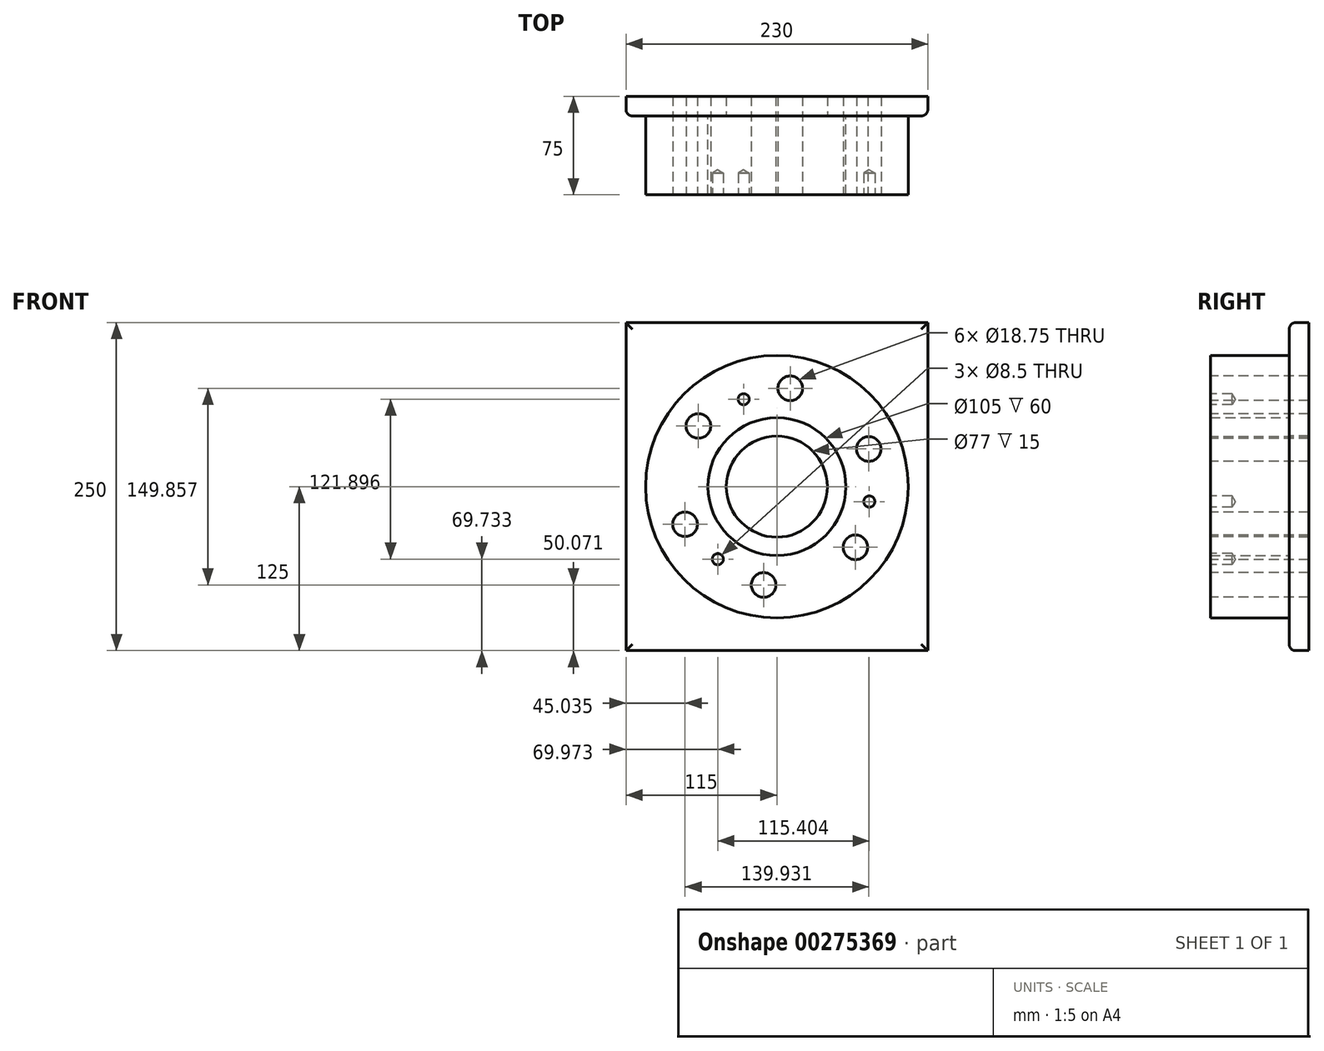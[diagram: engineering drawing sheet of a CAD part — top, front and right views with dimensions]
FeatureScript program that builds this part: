
annotation { "Feature Type Name" : "Feature", "Feature Type Description" : "" }
export const myFeature = defineFeature(function(context is Context, id is Id, definition is map)
    precondition{}
    {
        {
            var Q0;
            Q0=qCreatedBy(makeId("Front.planeOp"),FACE);
            var sketch = newSketch(context, id + "F0", { "sketchPlane" : qUnion([Q0])});
            skCircle(sketch, "E0", {"center": v(0, 0) * mm, "radius": 100 * mm});
            skCircle(sketch, "E1", {"center": v(0, 0) * mm, "radius": 52.5 * mm});
            skSolve(sketch);
        }
        {
            var Q0;
            Q0 = qSketchRegion(id + "F0", true);
            extrude(context, id + "F1", {"entities" : qUnion([Q0]), "depth" : 60 * mm});
        }
        {
            var Q0;
            Q0=makeQuery(id+"F1.opExtrude","CAP_FACE",FACE,{"disambiguationData":[OSD([sQuery(id+"F0.wireOp",EDGE,"E0"),sQuery(id+"F0.wireOp",EDGE,"E1")])],"isStart":false});
            var sketch = newSketch(context, id + "F2", { "sketchPlane" : qUnion([Q0])});
            skCircle(sketch, "E2", {"center": v(-59.81, 46.25) * mm, "radius": 9.38 * mm});
            skCircle(sketch, "E3.1.0", {"center": v(-69.97, -28.67) * mm, "radius": 9.38 * mm});
            skCircle(sketch, "E3.2.0", {"center": v(-10.15, -74.93) * mm, "radius": 9.38 * mm});
            skCircle(sketch, "E3.3.0", {"center": v(59.81, -46.25) * mm, "radius": 9.38 * mm});
            skCircle(sketch, "E3.4.0", {"center": v(69.97, 28.67) * mm, "radius": 9.38 * mm});
            skCircle(sketch, "E3.5.0", {"center": v(10.15, 74.93) * mm, "radius": 9.38 * mm});
            skPoint(sketch, "E3.center", {"position": v(0, 0) * mm});
            skSolve(sketch);
        }
        {
            var Q0;
            Q0=makeQuery(id+"F1.opExtrude","CAP_FACE",FACE,{"disambiguationData":[OSD([sQuery(id+"F0.wireOp",EDGE,"E0"),sQuery(id+"F0.wireOp",EDGE,"E1")])],"isStart":true});
            var sketch = newSketch(context, id + "F3", { "sketchPlane" : qUnion([Q0])});
            skLineSegment(sketch, "E4.bottom", {"start": v(-115, -125) * mm, "end": v(115, -125) * mm});
            skLineSegment(sketch, "E4.top", {"start": v(-115, 125) * mm, "end": v(115, 125) * mm});
            skLineSegment(sketch, "E4.left", {"start": v(-115, -125) * mm, "end": v(-115, 125) * mm});
            skLineSegment(sketch, "E4.right", {"start": v(115, -125) * mm, "end": v(115, 125) * mm});
            skSolve(sketch);
        }
        {
            var Q0;
            Q0 = qSketchRegion(id + "F3", true);
            extrude(context, id + "F4", {"entities" : qUnion([Q0]), "operationType" : NewBodyOperationType.ADD, "depth" : 15 * mm});
        }
        {
            var Q0;
            Q0 = qSketchRegion(id + "F2", true);
            extrude(context, id + "F5", {"entities" : qUnion([Q0]), "operationType" : NewBodyOperationType.REMOVE, "endBound" : BoundingType.THROUGH_ALL, "oppositeDirection" : true, "depth" : 25 * mm});
        }
        {
            var Q0;
            Q0=makeQuery(id+"F4.boolean.opBoolean","SPLIT",FACE,{"disambiguationData":[TD([makeQuery(id+"F1.opExtrude","SWEPT_FACE",FACE,{"disambiguationData":[OSD([sQuery(id+"F0.wireOp",EDGE,"E1")])]})])],"derivedFrom":makeQuery(id+"F4.opExtrude","CAP_FACE",FACE,{"disambiguationData":[OSD([sQuery(id+"F3.wireOp",EDGE,"E4.bottom"),sQuery(id+"F3.wireOp",EDGE,"E4.top"),sQuery(id+"F3.wireOp",EDGE,"E4.left"),sQuery(id+"F3.wireOp",EDGE,"E4.right")])],"isStart":true})});
            var sketch = newSketch(context, id + "F6", { "sketchPlane" : qUnion([Q0])});
            skCircle(sketch, "E5", {"center": v(0, 0) * mm, "radius": 38.5 * mm});
            skSolve(sketch);
        }
        {
            var Q0;
            Q0 = qSketchRegion(id + "F6", true);
            extrude(context, id + "F7", {"entities" : qUnion([Q0]), "operationType" : NewBodyOperationType.REMOVE, "endBound" : BoundingType.THROUGH_ALL, "oppositeDirection" : true, "depth" : 25 * mm});
        }
        {
            var Q0;
            Q0=makeQuery(id+"F1.opExtrude","CAP_FACE",FACE,{"disambiguationData":[OSD([sQuery(id+"F0.wireOp",EDGE,"E0"),sQuery(id+"F0.wireOp",EDGE,"E1")])],"isStart":false});
            var sketch = newSketch(context, id + "F8", { "sketchPlane" : qUnion([Q0])});
            skPoint(sketch, "E6", {"position": v(-45.03, -55.27) * mm});
            skPoint(sketch, "E7.1.0", {"position": v(70.38, -11.36) * mm});
            skPoint(sketch, "E7.2.0", {"position": v(-25.35, 66.63) * mm});
            skPoint(sketch, "E7.center", {"position": v(0, 0) * mm});
            skSolve(sketch);
        }
        {
            var Q0;
            Q0=sQuery(id+"F8.wireOp",VERTEX,"E6");
            var Q1;
            Q1=sQuery(id+"F8.wireOp",VERTEX,"E7.2.0");
            var Q2;
            Q2=sQuery(id+"F8.wireOp",VERTEX,"E7.1.0");
            var Q3;
            Q3=makeQuery(id+"F1.opExtrude","SWEPT_BODY",BODY,{"disambiguationData":[OSD([sQuery(id+"F0.wireOp",EDGE,"E0"),sQuery(id+"F0.wireOp",EDGE,"E1")])]});
            hole(context, id + "F9", {"style" : HoleStyle.SIMPLE, "endStyle" : HoleEndStyle.BLIND, "standardTappedOrClearance" : lookupTablePath({ "standard" : "ISO", "engagement" : "75%", "pitch" : "1.5 mm", "size" : "M10", "type" : "Tapped" }), "standardBlindInLast" : lookupTablePath({ "standard" : "ISO", "engagement" : "75%", "pitch" : "1.5 mm", "size" : "M10", "type" : "Tapped" }), "holeDiameter" : 8.5 * mm, "showTappedDepth" : true, "holeDepth" : 16.5 * mm, "tappedDepth" : 12 * mm, "tapClearance" : 3, "startFromSketch" : true, "locations" : qUnion([Q0, Q1, Q2]), "scope" : qUnion([Q3]), "majorDiameter" : 10 * mm});
        }
        {
            var Q0;
            Q0=makeQuery(id+"F4.opExtrude","CAP_EDGE",EDGE,{"disambiguationData":[OSD([sQuery(id+"F3.wireOp",EDGE,"E4.top")])],"isStart":true});
            var Q1;
            Q1=makeQuery(id+"F4.opExtrude","CAP_EDGE",EDGE,{"disambiguationData":[OSD([sQuery(id+"F3.wireOp",EDGE,"E4.left")])],"isStart":true});
            var Q2;
            Q2=makeQuery(id+"F4.opExtrude","CAP_EDGE",EDGE,{"disambiguationData":[OSD([sQuery(id+"F3.wireOp",EDGE,"E4.bottom")])],"isStart":true});
            var Q3;
            Q3=makeQuery(id+"F4.opExtrude","CAP_EDGE",EDGE,{"disambiguationData":[OSD([sQuery(id+"F3.wireOp",EDGE,"E4.right")])],"isStart":true});
            fillet(context, id + "F10", {"entities" : qUnion([Q0, Q1, Q2, Q3]), "radius" : 5 * mm, "tangentPropagation" : true, "allowEdgeOverflow" : false});
        }
    });
